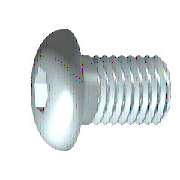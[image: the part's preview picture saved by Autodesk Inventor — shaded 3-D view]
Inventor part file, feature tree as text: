
AUTODESK INVENTOR PART (.ipt)
format: ipt  version: 2024 (Build 280153000, 153)  size: 189,952 bytes
history: native  units: mm (DEFAULTED — no unit token found)
features: extrude x1, plane x1, fillet x1
ambient origin geometry x7: Origin, YZ Plane, XY Plane, X Axis, Y Axis, Z Axis, Center Point
bodies: Solid1 (feature_tree), Body (feature_tree)
feature tree (3):
  extrude  "Slot"  Depth=14.5mm
  plane  "Work Plane1"
  fillet  "Fillet2"  Radius=0.306825mm
